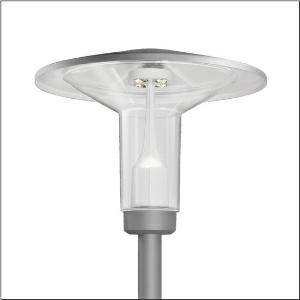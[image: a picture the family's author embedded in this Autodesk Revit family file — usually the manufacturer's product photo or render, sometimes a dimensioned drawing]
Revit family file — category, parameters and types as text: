
# Revit family: laterne_iq___st1_2a_5xa5255af14h_83bc
name_source: partatom
category: Lighting Fixtures
units: mm (PartAtom-declared; Revit-internal decimal feet)

## family parameters
Cut with Voids When Loaded = No
Host = Face
Light Source = No
Part Type = Normal
Room Calculation Point = No
Round Connector Dimension = Use Diameter
Shared = No

## types (1)
- --- (1 x LED, 1540 lm, 12.9 W, 2200K)
    Apparent Load = 13 VA
    CIE Flux Codes = 25 63 94 98 100
    Color Rendering = 70
    Color Temperature = 2200K
    Default Elevation = 1800 mm
    Description = Lantern iQ, mast luminaire, Module 540 iQ-SR, primary light control with 3 zone facetted reflector, of plastic, silver coated, highly specular, structured, primary optical cover: cover, of PMMA, transparent, light distribution: ST1.2a, light emission: direct distribution, primary light characteristic: asymmetric, installation type: post-top, LED, High Power LED, rated luminous flux: 1.540lm, luminous efficacy: 119lm/W, light colour: 722, colour temperature: 2200K, control gear: ECG iQ, control: presetting dimming logarithmic, Street-Remote, Auto-Match, Temp-Guard, Lumen-Switch, Night-Set, Smart-Wire, Light-Fading, Desk-Remote (wireless, voltage-free reading and setting of iQ features in the workshop via application-optimized NFC function/RFID function), optimised constant luminous flux control (CLO 2.0), with terminal, 6-pole, max. 2.5mm², mains connection: 230..240V, AC, 50/60Hz, start of lifetime: 13W, end of service life: 13W, reduction: 6W, luminaire housing, upper part, of glass-fibre reinforced polyester, coated, Siteco® metallic grey (DB 702S), diameter: 750mm, height: 583mm, spigot size: d x l = 76 x 70mm (post-top) | with reducer (optional accessory) 60 x 70mm, post-top mast mounting element, of diecast aluminium, coated, Siteco® metallic grey (DB 702S), Module 540 iQ-SR, traffic white (RAL 9016), equipment: standard, protection rating (complete): IP65, insulation class (complete): insulation class II (safety insulation), certification: CE, ENEC, VDE, packaging unit: 1 piece

Light Distribution: ST1.2a
    Height = 583 mm
    Lamp = 1 x LED
    Lamp Light Flux = 1540 lm
    Lamp Power = 12.9 W
    Lamp count = 1
    Length = 750 mm
    Luminous efficacy = 119 lm/W
    Manufacturer = Siteco
    ModVariant = No
    Model = 5XA5255AF14H
    Number of Poles = 1
    OnlyDefault = Yes
    Power Factor = 1
    Product Name = Laterne iQ | ST1.2a
    Product group = mast luminaire | pylon top
    ProductGroupID = 6100
    Protection Class = Protection class II
    Protection Degree = IP 65
    RLX_Detail_Level = 1
    RLX_Emergency_Light_Flux = 0 lm
    RLX_Emergency_Type = 0
    RLX_Emergency_Type_DB = No
    RlxData = <blob elided: 103953 chars, md5=2442a773>
    Socket = socket
    Standby Power = 0 W
    System Light Flux = 1540 lm
    System Power = 13 W
    Type Comments = factory setting: luminous flux: 100 % | dim-lin: 254 | 516 mA
    Type Image = l_1006050.jpg
    URL = http://relux.com
    VarID = @adj_110843
    Voltage = 0 V
    Weight = 0.00 kg
    Width = 0 mm  [stored 0 ft]

note: [stored X ft] marks values corroborated as IEEE doubles in the binary element streams (Revit-internal decimal feet)

## geometry (parser evidence)
native form markers: Blend x4, Sweep x10
no freeform markers — native parametric forms only
